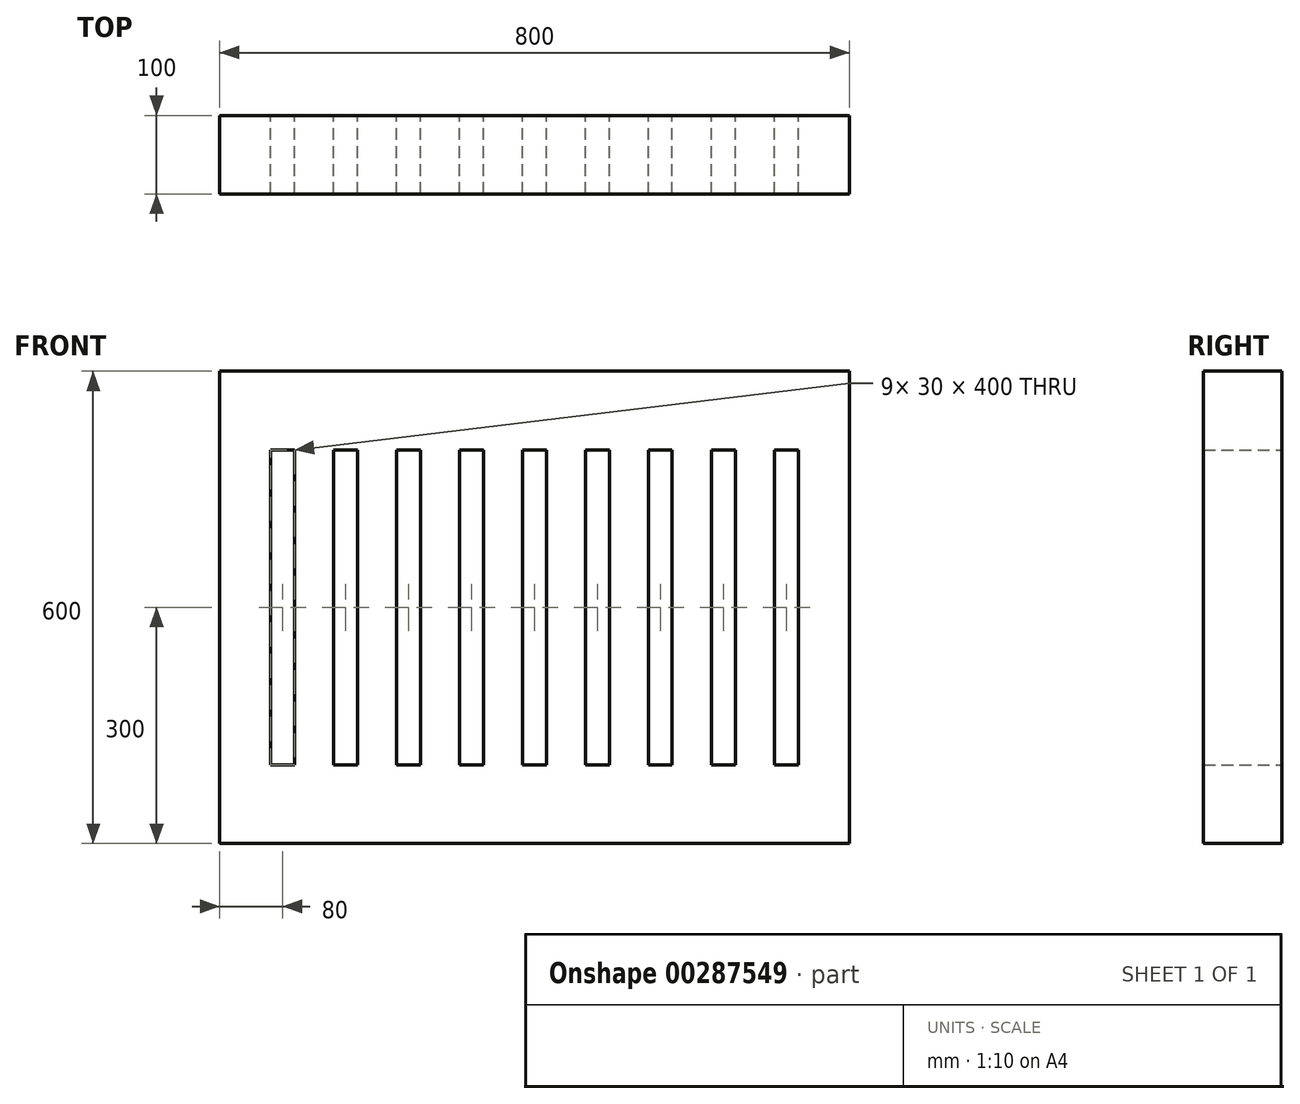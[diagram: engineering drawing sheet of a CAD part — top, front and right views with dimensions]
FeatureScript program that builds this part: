
annotation { "Feature Type Name" : "Feature", "Feature Type Description" : "" }
export const myFeature = defineFeature(function(context is Context, id is Id, definition is map)
    precondition{}
    {
        {
            var Q0;
            Q0=qCreatedBy(makeId("Front.planeOp"),FACE);
            var sketch = newSketch(context, id + "F0", { "sketchPlane" : qUnion([Q0])});
            skLineSegment(sketch, "E0.bottom", {"start": v(0, -50) * mm, "end": v(800, -50) * mm});
            skLineSegment(sketch, "E0.top", {"start": v(0, 550) * mm, "end": v(800, 550) * mm});
            skLineSegment(sketch, "E0.left", {"start": v(0, -50) * mm, "end": v(0, 550) * mm});
            skLineSegment(sketch, "E0.right", {"start": v(800, -50) * mm, "end": v(800, 550) * mm});
            skLineSegment(sketch, "E1.bottom", {"start": v(65, 450) * mm, "end": v(95, 450) * mm});
            skLineSegment(sketch, "E1.top", {"start": v(65, 50) * mm, "end": v(95, 50) * mm});
            skLineSegment(sketch, "E1.left", {"start": v(65, 450) * mm, "end": v(65, 50) * mm});
            skLineSegment(sketch, "E1.right", {"start": v(95, 450) * mm, "end": v(95, 50) * mm});
            skLineSegment(sketch, "E2.1.0.0", {"start": v(145, 450) * mm, "end": v(145, 50) * mm});
            skLineSegment(sketch, "E2.1.0.1", {"start": v(175, 450) * mm, "end": v(175, 50) * mm});
            skLineSegment(sketch, "E2.1.0.2", {"start": v(145, 50) * mm, "end": v(175, 50) * mm});
            skLineSegment(sketch, "E2.1.0.3", {"start": v(145, 450) * mm, "end": v(175, 450) * mm});
            skLineSegment(sketch, "E2.2.0.0", {"start": v(225, 450) * mm, "end": v(225, 50) * mm});
            skLineSegment(sketch, "E2.2.0.1", {"start": v(255, 450) * mm, "end": v(255, 50) * mm});
            skLineSegment(sketch, "E2.2.0.2", {"start": v(225, 50) * mm, "end": v(255, 50) * mm});
            skLineSegment(sketch, "E2.2.0.3", {"start": v(225, 450) * mm, "end": v(255, 450) * mm});
            skLineSegment(sketch, "E2.3.0.0", {"start": v(305, 450) * mm, "end": v(305, 50) * mm});
            skLineSegment(sketch, "E2.3.0.1", {"start": v(335, 450) * mm, "end": v(335, 50) * mm});
            skLineSegment(sketch, "E2.3.0.2", {"start": v(305, 50) * mm, "end": v(335, 50) * mm});
            skLineSegment(sketch, "E2.3.0.3", {"start": v(305, 450) * mm, "end": v(335, 450) * mm});
            skLineSegment(sketch, "E2.4.0.0", {"start": v(385, 450) * mm, "end": v(385, 50) * mm});
            skLineSegment(sketch, "E2.4.0.1", {"start": v(415, 450) * mm, "end": v(415, 50) * mm});
            skLineSegment(sketch, "E2.4.0.2", {"start": v(385, 50) * mm, "end": v(415, 50) * mm});
            skLineSegment(sketch, "E2.4.0.3", {"start": v(385, 450) * mm, "end": v(415, 450) * mm});
            skLineSegment(sketch, "E2.5.0.0", {"start": v(465, 450) * mm, "end": v(465, 50) * mm});
            skLineSegment(sketch, "E2.5.0.1", {"start": v(495, 450) * mm, "end": v(495, 50) * mm});
            skLineSegment(sketch, "E2.5.0.2", {"start": v(465, 50) * mm, "end": v(495, 50) * mm});
            skLineSegment(sketch, "E2.5.0.3", {"start": v(465, 450) * mm, "end": v(495, 450) * mm});
            skLineSegment(sketch, "E2.6.0.0", {"start": v(545, 450) * mm, "end": v(545, 50) * mm});
            skLineSegment(sketch, "E2.6.0.1", {"start": v(575, 450) * mm, "end": v(575, 50) * mm});
            skLineSegment(sketch, "E2.6.0.2", {"start": v(545, 50) * mm, "end": v(575, 50) * mm});
            skLineSegment(sketch, "E2.6.0.3", {"start": v(545, 450) * mm, "end": v(575, 450) * mm});
            skLineSegment(sketch, "E2.7.0.0", {"start": v(625, 450) * mm, "end": v(625, 50) * mm});
            skLineSegment(sketch, "E2.7.0.1", {"start": v(655, 450) * mm, "end": v(655, 50) * mm});
            skLineSegment(sketch, "E2.7.0.2", {"start": v(625, 50) * mm, "end": v(655, 50) * mm});
            skLineSegment(sketch, "E2.7.0.3", {"start": v(625, 450) * mm, "end": v(655, 450) * mm});
            skLineSegment(sketch, "E2.8.0.0", {"start": v(705, 450) * mm, "end": v(705, 50) * mm});
            skLineSegment(sketch, "E2.8.0.1", {"start": v(735, 450) * mm, "end": v(735, 50) * mm});
            skLineSegment(sketch, "E2.8.0.2", {"start": v(705, 50) * mm, "end": v(735, 50) * mm});
            skLineSegment(sketch, "E2.8.0.3", {"start": v(705, 450) * mm, "end": v(735, 450) * mm});
            skLineSegment(sketch, "E2.direction1", {"start": v(65, 50) * mm, "end": v(145, 50) * mm, "construction": true});
            skSolve(sketch);
        }
        {
            var Q0;
            Q0 = qSketchRegion(id + "F0", true);
            extrude(context, id + "F1", {"entities" : qUnion([Q0]), "endBound" : BoundingType.SYMMETRIC, "depth" : 100 * mm, "offsetDistance" : 25 * mm});
        }
    });
